# Revit family: Furniture_Other_Sjobergs_Workbench_Junior&Senior
name_source: partatom
category: Furniture
revit_build: Autodesk Revit 2017 (Build: 20160225_1515(x64)
units: mm (PartAtom-declared; Revit-internal decimal feet)

## family parameters
Always vertical = Yes
Cut with Voids When Loaded = No
OmniClass Number = 23.40.70.14
OmniClass Title = Retail and Commercial Equipment and Furnishings
Room Calculation Point = No
Shared = No
Work Plane-Based = No

## types (2) — shared parameters
AssetType = Movable
BIMObjectName = Furniture_Other_Sjobergs_Workbench_Junior&Senior
Brand = Sjöbergs
Category = Hobby
Collection = Planer Benches
Color = Wooden
ConvergoRefNr = 0184-2005-0019-SE
Description = Intended for pre-school and recreational activities. Junior&Senior is delivered complete with trestle and bench dogs. Trestle is delivered in 640 and 860 mm.
DurationUnit = Year
Features = A sturdy bench with many features that facilitate woodworking and crafts. The bench has two double rows of bench dog holes. Cupboard 0022 only suits the Senior height.
Finish = Solid birch
IfcExportAs = IfcFurnishingElementType
IfcExportType = TABLE
MainColor = Wooden
Manufacturer = Sjöbergs
ManufacturerName = Sjöbergs
ManufacturerURL = https://www.sjobergs.se
Material = Wood, metal
ModelReference = 33365
NBSDescription = School art, design and technology tables and workbenches;
NBSReference = 45-35-20/320
Name = Sjobergs_Workbench_Junior&Senior
NominalDepth = 490 mm
NominalLength = 1000 mm  [stored 3.28084 ft]
ProductDatasheet = https://www.sjobergs.se
ProductInformation = Intended for pre-school and recreational activities. Junior&Senior is delivered complete with trestle and bench dogs. Trestle is delivered in 640 and 860 mm.
Shape = Sculptured
TableMainMaterial = Beech
TableSecondaryMaterial = Black Metal
URL = https://www.sjobergs.se
Uniclass2 = Pr_40_50_21
Uniclass2015Description = Desks, Tables And Worktops
Uniclass2015Reference = Pr_40_50_21_76
Version = 1
VersionDate = 26/06/2020
WarrantyDurationUnit = Year
Weight = 22 kg
zero-valued in all types: Cost

## per-type parameters (varying)
| type | Constituents | ModelType | Size |
| 33365 Sjobergs Bench Junior | 33365 Junior | 33365_Junior | 1000x490x640 mm |
| 33365 Sjobergs Bench Senior | 33365 Senior | 33365_Senior | 1000x490x860 mm |

note: column(s) folded — value = type name in every type: Model

note: [stored X ft] marks values corroborated as IEEE doubles in the binary element streams (Revit-internal decimal feet)

## geometry (parser evidence)
native form markers: Sweep x11
no freeform markers — native parametric forms only
